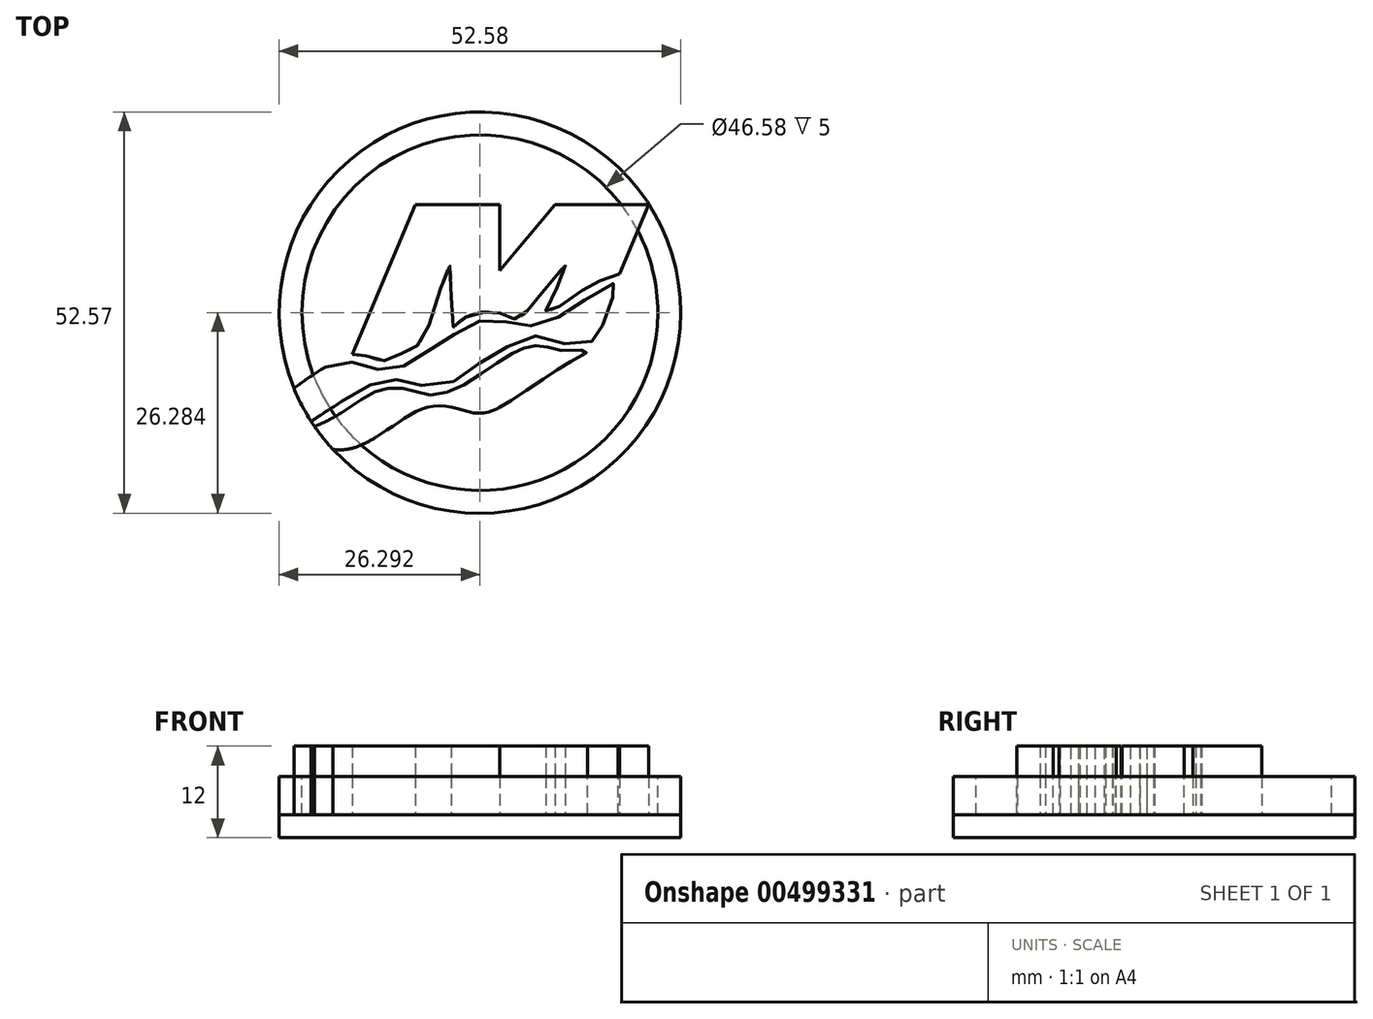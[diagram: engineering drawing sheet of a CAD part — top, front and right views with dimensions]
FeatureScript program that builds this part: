
annotation { "Feature Type Name" : "Feature", "Feature Type Description" : "" }
export const myFeature = defineFeature(function(context is Context, id is Id, definition is map)
    precondition{}
    {
        {
            var Q0;
            Q0=qCreatedBy(makeId("Top.planeOp"),FACE);
            var sketch = newSketch(context, id + "F0", { "sketchPlane" : qUnion([Q0])});
            skFitSpline(sketch, "E0", {"points": [v(4.48, 24.19) * mm, v(0.1, 23.6) * mm, v(-2.9, 22.8) * mm, v(-6.05, 21.25) * mm, v(-10.09, 18.35) * mm, v(-12.98, 15.6) * mm, v(-14.23, 14) * mm, v(-15.73, 11.61) * mm, v(-17.32, 7.87) * mm, v(-18.22, 3.73) * mm, v(-18.27, -0.11) * mm, v(-17.57, -6) * mm, v(-17.27, -7.2) * mm], "startDerivative": vector(-49.66, -5.79) * mm, "endDerivative": vector(5.77, -18.57) * mm});
            skFitSpline(sketch, "E1", {"points": [v(-23.66, -11.14) * mm, v(-21.37, -10.54) * mm, v(-18.32, -8.8) * mm, v(-16.03, -7.2) * mm, v(-13.33, -5.7) * mm, v(-11.04, -5.5) * mm, v(-9.14, -5.95) * mm, v(-6.05, -6.65) * mm, v(-4.05, -5.95) * mm, v(-1.6, -4.5) * mm, v(0.84, -2.9) * mm, v(3.99, -0.96) * mm, v(6.28, -0.01) * mm, v(8.83, -0.06) * mm, v(10.77, -0.66) * mm, v(13.07, -0.66) * mm, v(15.86, 0.24) * mm, v(18.66, 1.98) * mm, v(21.8, 4.08) * mm, v(23.95, 4.88) * mm, v(23.6, 3.78) * mm, v(22.65, 1.18) * mm, v(21.6, -1.51) * mm, v(21.2, -2.4) * mm, v(19.36, -3.1) * mm, v(16.66, -3) * mm, v(13.57, -2.06) * mm, v(10.77, -2.8) * mm, v(7.58, -4.56) * mm, v(4.48, -6.6) * mm, v(1.74, -8.35) * mm, v(-1.9, -8.5) * mm, v(-4.15, -7.9) * mm, v(-6.24, -7.85) * mm, v(-8.94, -8.7) * mm, v(-12.18, -10.64) * mm, v(-15.28, -12.64) * mm, v(-16.63, -13.39) * mm, v(-19.92, -13.29) * mm, v(-23.66, -11.14) * mm]});
            skLineSegment(sketch, "E2", {"start": v(-2.6, 15.1) * mm, "end": v(-10.84, -4.46) * mm});
            skLineSegment(sketch, "E3", {"start": v(-2.6, 15.1) * mm, "end": v(8.48, 15.1) * mm});
            skLineSegment(sketch, "E4", {"start": v(8.48, 15.1) * mm, "end": v(8.48, 6.47) * mm});
            skLineSegment(sketch, "E5", {"start": v(8.48, 6.47) * mm, "end": v(15.71, 15.1) * mm});
            skLineSegment(sketch, "E6", {"start": v(15.71, 15.1) * mm, "end": v(27.99, 15.1) * mm});
            skLineSegment(sketch, "E7", {"start": v(27.99, 15.1) * mm, "end": v(24.18, 6.06) * mm});
            skFitSpline(sketch, "E8", {"points": [v(-10.84, -4.46) * mm, v(-9.54, -4.46) * mm, v(-7.1, -5.35) * mm, v(-4.55, -4.46) * mm, v(-2.45, -3.46) * mm, v(-0.26, 1.03) * mm, v(1.99, 7.02) * mm, v(2.34, -0.81) * mm, v(3.24, -0.16) * mm, v(5.88, 0.98) * mm, v(7.68, 1.03) * mm, v(9.72, 0.58) * mm, v(10.87, 0.09) * mm, v(13.02, 2.43) * mm, v(15.61, 5.48) * mm, v(17.01, 7.22) * mm, v(16.21, 4.73) * mm, v(14.57, 0.98) * mm, v(18, 3.08) * mm, v(21.15, 4.98) * mm, v(24.18, 6.06) * mm], "startDerivative": vector(36.8, 6.68) * mm, "endDerivative": vector(60.95, 19.52) * mm});
            skFitSpline(sketch, "E9", {"points": [v(4.48, 24.19) * mm, v(6.82, 24.19) * mm, v(11.63, 23.28) * mm, v(16.73, 21.08) * mm, v(20.83, 18.05) * mm, v(23.8, 15.1) * mm], "startDerivative": vector(14.46, 0.7) * mm, "endDerivative": vector(14.33, -15.04) * mm});
            skFitSpline(sketch, "E10", {"points": [v(26.09, 10.59) * mm, v(27.31, 8.63) * mm, v(28.44, 4.18) * mm, v(27.95, -5.84) * mm, v(24.7, -12.9) * mm, v(18.2, -19.32) * mm, v(9.74, -22.71) * mm, v(2.82, -23.06) * mm, v(-5.15, -20.95) * mm, v(-11.15, -16.85) * mm], "startDerivative": vector(20.15, -28.06) * mm, "endDerivative": vector(-49.3, 39.91) * mm});
            skFitSpline(sketch, "E11", {"points": [v(4.96, 21.22) * mm, v(1.87, 20.92) * mm, v(-2.64, 19.68) * mm, v(-8.63, 15.88) * mm, v(-12.96, 10.59) * mm, v(-14.62, 6.06) * mm, v(-15.28, 3.06) * mm, v(-15.28, -1.98) * mm, v(-14.5, -5.43) * mm, v(-11.72, -11.42) * mm, v(-7.35, -15.74) * mm, v(-0.3, -19.41) * mm, v(7.4, -19.98) * mm, v(13.75, -18.36) * mm, v(20.42, -13.03) * mm, v(23.77, -7.84) * mm, v(25.46, -2.48) * mm, v(25.59, 1.99) * mm, v(24.8, 6.47) * mm], "startDerivative": vector(-71.76, -4.74) * mm, "endDerivative": vector(-19.14, 89.8) * mm});
            skFitSpline(sketch, "E12", {"points": [v(4.96, 21.22) * mm, v(9.05, 20.8) * mm, v(13.54, 19.2) * mm, v(17.61, 16.68) * mm, v(19.29, 15.1) * mm], "startDerivative": vector(15.9, -0.84) * mm, "endDerivative": vector(7.53, -7.9) * mm});
            skFitSpline(sketch, "E13", {"points": [v(-17.57, -14.65) * mm, v(-14.52, -13.39) * mm, v(-11.54, -11.68) * mm, v(-8.4, -9.68) * mm, v(-6, -8.88) * mm, v(-3.33, -9.1) * mm, v(-0.87, -9.8) * mm, v(2.84, -8.95) * mm, v(7, -6.35) * mm, v(10.6, -4.1) * mm, v(12.35, -3.45) * mm, v(14.28, -3.39) * mm, v(16.54, -3.97) * mm, v(19.98, -4.02) * mm, v(17.55, -5.53) * mm, v(14.93, -7.2) * mm, v(10.75, -10) * mm, v(8.48, -11.42) * mm], "startDerivative": vector(51.37, 19.43) * mm, "endDerivative": vector(-37.28, -22.82) * mm});
            skFitSpline(sketch, "E14", {"points": [v(8.48, -11.42) * mm, v(7.12, -12.01) * mm, v(4.96, -12.14) * mm, v(2.3, -11.42) * mm, v(-0.98, -11.42) * mm, v(-4.2, -13) * mm, v(-7.83, -15.4) * mm, v(-11.15, -16.85) * mm, v(-14.34, -16.67) * mm, v(-17.57, -14.65) * mm], "startDerivative": vector(-16.31, -8.64) * mm, "endDerivative": vector(-25.48, 19.6) * mm});
            skCircle(sketch, "E15", {"center": v(5.88, 0.98) * mm, "radius": 26.29 * mm});
            skLineSegment(sketch, "E16", {"start": v(-26.73, 31.69) * mm, "end": v(34.95, 31.69) * mm});
            skLineSegment(sketch, "E17", {"start": v(34.95, 31.69) * mm, "end": v(34.95, -30) * mm});
            skLineSegment(sketch, "E18", {"start": v(-26.73, -30) * mm, "end": v(-26.73, 31.69) * mm});
            skSolve(sketch);
        }
        {
            var Q0;
            Q0=makeQuery(id+"F0.imprint","IMPRINT",FACE,{"disambiguationData":[TD([[makeQuery(id+"F0.imprint","IMPRINT",EDGE,{"derivedFrom":sQuery(id+"F0.wireOp",EDGE,"E2")}),1.0]])]});
            var Q1;
            {var subQ0=sQuery(id+"F0.wireOp",EDGE,"E11");var subQ1=sQuery(id+"F0.wireOp",EDGE,"E1");var subQ2=makeQuery(id+"F0.imprint","INTERSECT",VERTEX,{"disambiguationData":[OD(0.0)],"derivedFrom":[subQ1,subQ0]});Q1=makeQuery(id+"F0.imprint","IMPRINT",FACE,{"disambiguationData":[TD([[makeQuery(id+"F0.imprint","IMPRINT",EDGE,{"disambiguationData":[TD([[subQ2,-1.0]])],"derivedFrom":subQ1}),-1.0]])]});}
            var Q2;
            {var subQ0=sQuery(id+"F0.wireOp",EDGE,"E11");var subQ1=sQuery(id+"F0.wireOp",EDGE,"E1");var subQ2=makeQuery(id+"F0.imprint","INTERSECT",VERTEX,{"disambiguationData":[OD(0.0)],"derivedFrom":[subQ1,subQ0]});Q2=makeQuery(id+"F0.imprint","IMPRINT",FACE,{"disambiguationData":[TD([[makeQuery(id+"F0.imprint","IMPRINT",EDGE,{"disambiguationData":[TD([[subQ2,1.0]])],"derivedFrom":subQ1}),-1.0]])]});}
            var Q3;
            {var subQ0=sQuery(id+"F0.wireOp",EDGE,"E13");var subQ1=sQuery(id+"F0.wireOp",EDGE,"E11");var subQ2=makeQuery(id+"F0.imprint","INTERSECT",VERTEX,{"derivedFrom":[subQ1,subQ0]});Q3=makeQuery(id+"F0.imprint","IMPRINT",FACE,{"disambiguationData":[TD([[makeQuery(id+"F0.imprint","IMPRINT",EDGE,{"disambiguationData":[TD([[subQ2,-1.0]])],"derivedFrom":subQ1}),-1.0]])]});}
            var Q4;
            {var subQ0=sQuery(id+"F0.wireOp",EDGE,"E13");var subQ1=sQuery(id+"F0.wireOp",EDGE,"E11");var subQ2=makeQuery(id+"F0.imprint","INTERSECT",VERTEX,{"derivedFrom":[subQ1,subQ0]});Q4=makeQuery(id+"F0.imprint","IMPRINT",FACE,{"disambiguationData":[TD([[makeQuery(id+"F0.imprint","IMPRINT",EDGE,{"disambiguationData":[TD([[subQ2,-1.0]])],"derivedFrom":subQ1}),1.0]])]});}
            extrude(context, id + "F1", {"entities" : qUnion([Q0, Q1, Q2, Q3, Q4]), "depth" : 5 * mm, "offsetDistance" : 25 * mm});
        }
        {
            var Q0;
            Q0=sQuery(id+"F0.wireOp",EDGE,"E15");
            extrude(context, id + "F2", {"bodyType" : ToolBodyType.SURFACE, "surfaceEntities" : qUnion([Q0]), "depth" : 5 * mm, "offsetDistance" : 25 * mm});
        }
        {
            var Q0;
            Q0=makeQuery(id+"F1.opExtrude","CAP_FACE",FACE,{"disambiguationData":[OSD([sQuery(id+"F0.wireOp",EDGE,"E2"),sQuery(id+"F0.wireOp",EDGE,"E3"),sQuery(id+"F0.wireOp",EDGE,"E4"),sQuery(id+"F0.wireOp",EDGE,"E5"),sQuery(id+"F0.wireOp",EDGE,"E6"),sQuery(id+"F0.wireOp",EDGE,"E7"),sQuery(id+"F0.wireOp",EDGE,"E8")])],"isStart":true});
            var sketch = newSketch(context, id + "F3", { "sketchPlane" : qUnion([Q0])});
            skCircle(sketch, "E19.0", {"center": v(5.88, -0.98) * mm, "radius": 26.29 * mm});
            skSolve(sketch);
        }
        {
            var Q0;
            Q0 = qSketchRegion(id + "F3", true);
            extrude(context, id + "F4", {"entities" : qUnion([Q0]), "depth" : 3 * mm, "offsetDistance" : 25 * mm});
        }
        {
            var Q0;
            Q0=makeQuery(id+"F1.opExtrude","CAP_FACE",FACE,{"disambiguationData":[OSD([sQuery(id+"F0.wireOp",EDGE,"E2"),sQuery(id+"F0.wireOp",EDGE,"E3"),sQuery(id+"F0.wireOp",EDGE,"E4"),sQuery(id+"F0.wireOp",EDGE,"E5"),sQuery(id+"F0.wireOp",EDGE,"E6"),sQuery(id+"F0.wireOp",EDGE,"E7"),sQuery(id+"F0.wireOp",EDGE,"E8")])],"isStart":false});
            var sketch = newSketch(context, id + "F5", { "sketchPlane" : qUnion([Q0])});
            skCircle(sketch, "E20.0", {"center": v(5.88, 0.98) * mm, "radius": 26.29 * mm});
            skCircle(sketch, "E21.0", {"center": v(5.88, 0.98) * mm, "radius": 23.29 * mm});
            skSolve(sketch);
        }
        {
            var Q0;
            Q0 = qSketchRegion(id + "F5", true);
            var Q1;
            Q1=makeQuery(id+"F4.opExtrude","CAP_FACE",FACE,{"disambiguationData":[OSD([sQuery(id+"F3.wireOp",EDGE,"E19.0")])],"isStart":true});
            extrude(context, id + "F6", {"entities" : qUnion([Q0]), "endBound" : BoundingType.UP_TO_SURFACE, "oppositeDirection" : true, "depth" : 25 * mm, "endBoundEntityFace" : qUnion([Q1]), "offsetDistance" : 25 * mm});
        }
        {
            var Q0;
            Q0=makeQuery(id+"F1.opExtrude","CAP_FACE",FACE,{"disambiguationData":[OSD([sQuery(id+"F0.wireOp",EDGE,"E2"),sQuery(id+"F0.wireOp",EDGE,"E3"),sQuery(id+"F0.wireOp",EDGE,"E4"),sQuery(id+"F0.wireOp",EDGE,"E5"),sQuery(id+"F0.wireOp",EDGE,"E6"),sQuery(id+"F0.wireOp",EDGE,"E7"),sQuery(id+"F0.wireOp",EDGE,"E8")])],"isStart":false});
            var Q1;
            Q1=makeQuery(id+"F1.opExtrude","CAP_FACE",FACE,{"disambiguationData":[OSD([sQuery(id+"F0.wireOp",EDGE,"E1"),sQuery(id+"F0.wireOp",EDGE,"E15")])],"isStart":false});
            var Q2;
            Q2=makeQuery(id+"F1.opExtrude","CAP_FACE",FACE,{"disambiguationData":[OSD([sQuery(id+"F0.wireOp",EDGE,"E13"),sQuery(id+"F0.wireOp",EDGE,"E14"),sQuery(id+"F0.wireOp",EDGE,"E15")])],"isStart":false});
            extrude(context, id + "F7", {"entities" : qUnion([Q0, Q1, Q2]), "depth" : 4 * mm, "offsetDistance" : 25 * mm});
        }
    });
